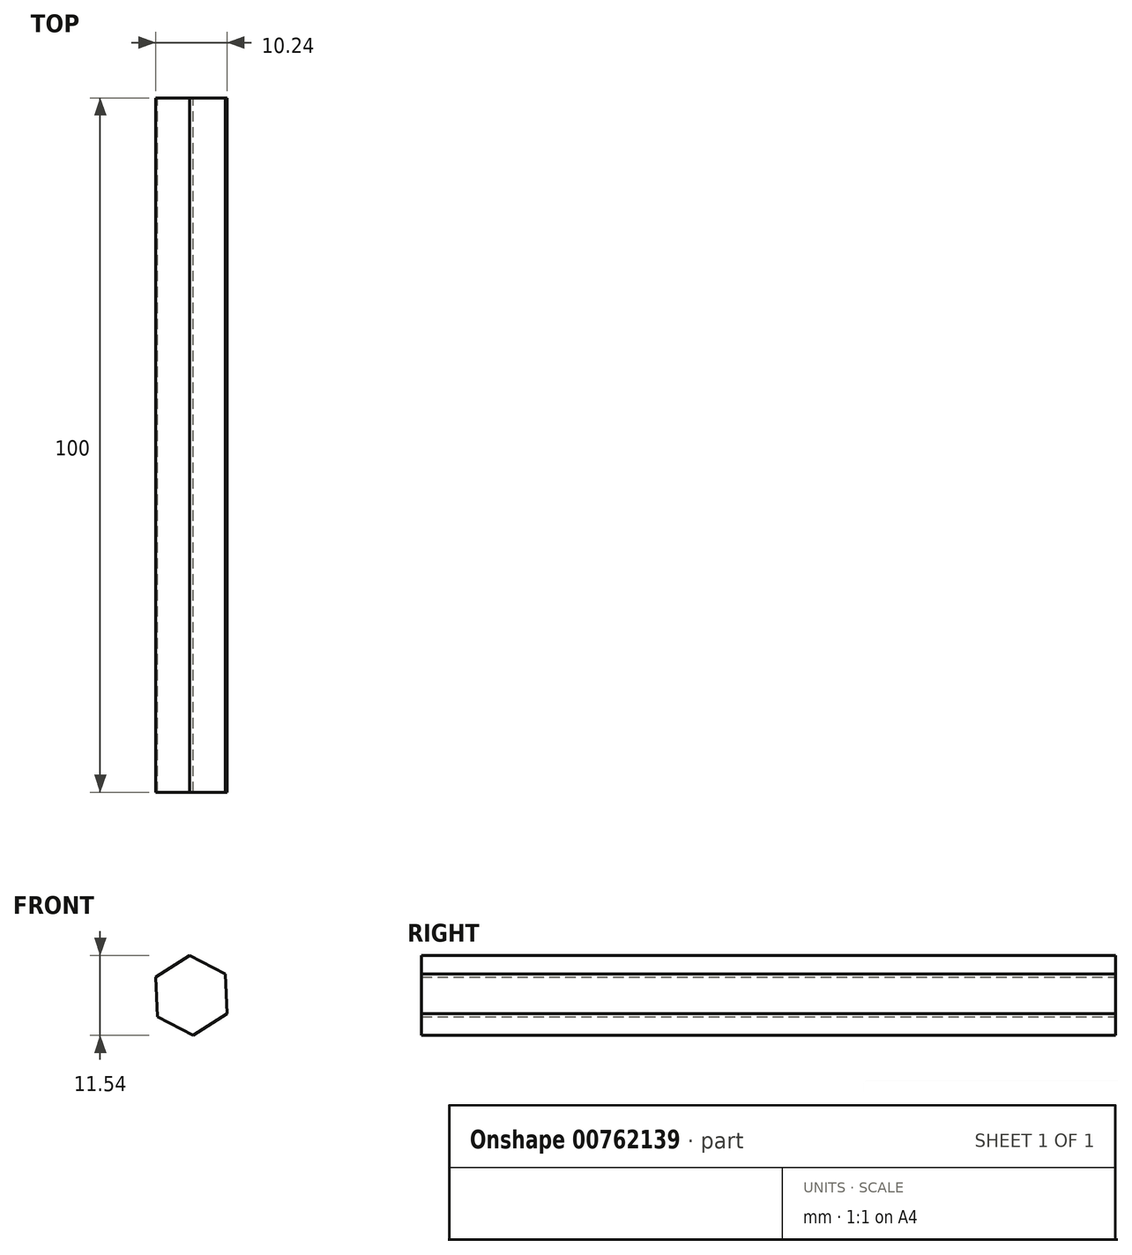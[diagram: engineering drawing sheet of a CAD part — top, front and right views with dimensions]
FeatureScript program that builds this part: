
annotation { "Feature Type Name" : "Feature", "Feature Type Description" : "" }
export const myFeature = defineFeature(function(context is Context, id is Id, definition is map)
    precondition{}
    {
        {
            var Q0;
            Q0=qCreatedBy(makeId("Front.planeOp"),FACE);
            var sketch = newSketch(context, id + "F0", { "sketchPlane" : qUnion([Q0])});
            skCircle(sketch, "E0.cCircle", {"center": v(0, 0) * mm, "radius": 5 * mm, "construction": true});
            skLineSegment(sketch, "E0.0", {"start": v(-5.12, 2.66) * mm, "end": v(-0.26, 5.77) * mm});
            skLineSegment(sketch, "E0.1", {"start": v(-0.26, 5.77) * mm, "end": v(4.87, 3.1) * mm});
            skLineSegment(sketch, "E0.2", {"start": v(4.87, 3.1) * mm, "end": v(5.12, -2.66) * mm});
            skLineSegment(sketch, "E0.3", {"start": v(5.12, -2.66) * mm, "end": v(0.26, -5.77) * mm});
            skLineSegment(sketch, "E0.4", {"start": v(0.26, -5.77) * mm, "end": v(-4.87, -3.1) * mm});
            skLineSegment(sketch, "E0.5", {"start": v(-4.87, -3.1) * mm, "end": v(-5.12, 2.66) * mm});
            skPoint(sketch, "E0.0.midPoint", {"position": v(-2.7, 4.21) * mm});
            skSolve(sketch);
        }
        {
            var Q0;
            Q0 = qSketchRegion(id + "F0", true);
            extrude(context, id + "F1", {"entities" : qUnion([Q0]), "depth" : 100 * mm, "offsetDistance" : 25 * mm});
        }
    });
